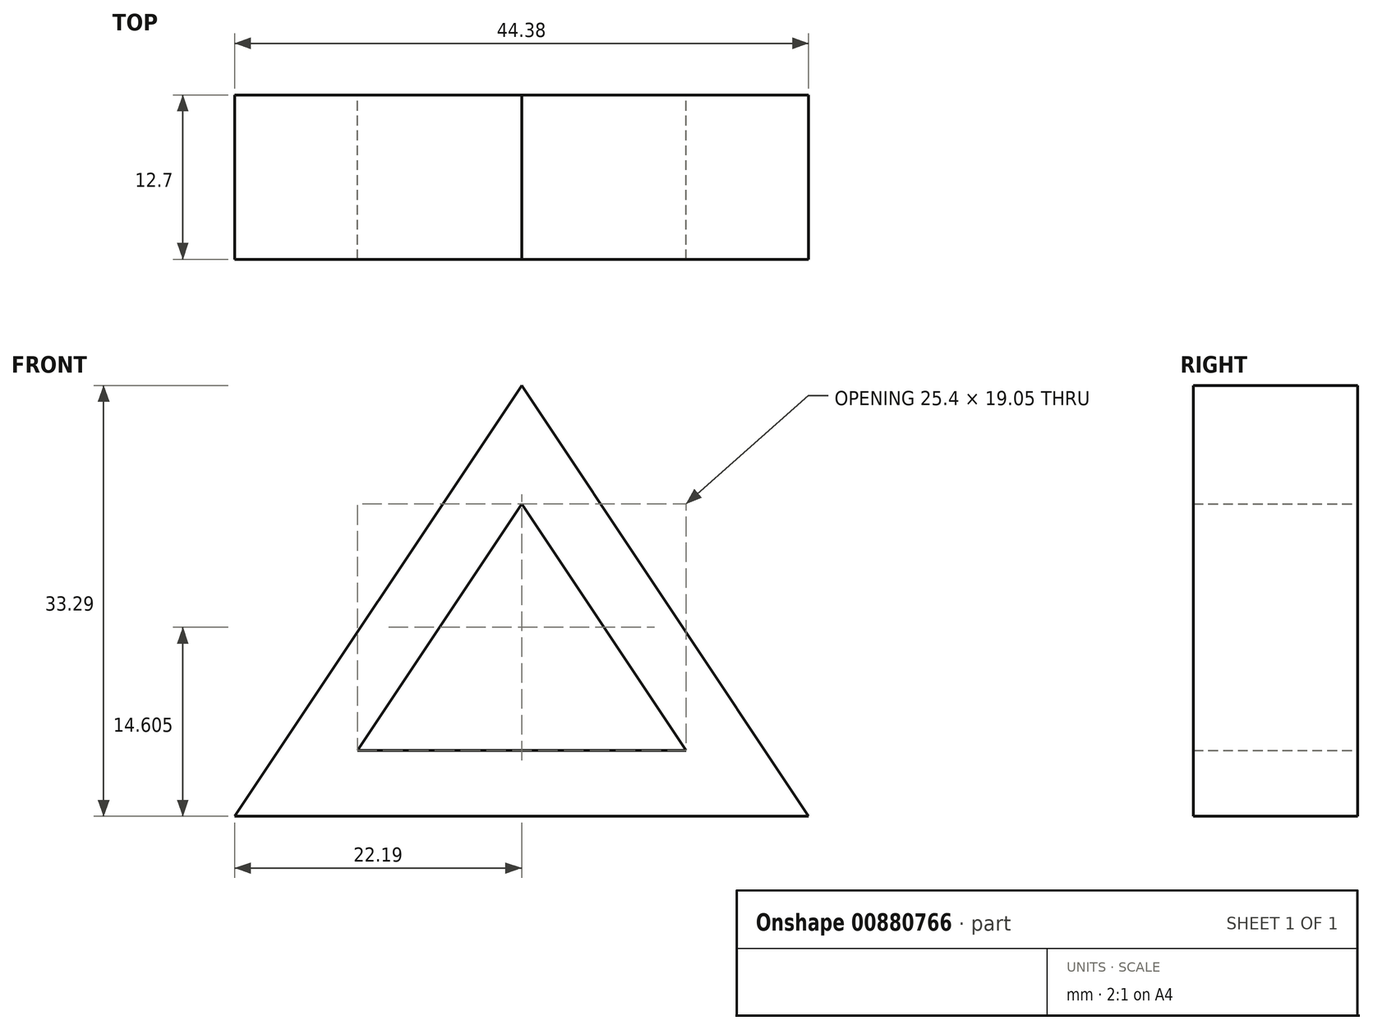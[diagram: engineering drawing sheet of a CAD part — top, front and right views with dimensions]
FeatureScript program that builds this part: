
annotation { "Feature Type Name" : "Feature", "Feature Type Description" : "" }
export const myFeature = defineFeature(function(context is Context, id is Id, definition is map)
    precondition{}
    {
        {
            var Q0;
            Q0=qCreatedBy(makeId("Front.planeOp"),FACE);
            var sketch = newSketch(context, id + "F0", { "sketchPlane" : qUnion([Q0])});
            skLineSegment(sketch, "E0", {"start": v(-12.7, 0) * mm, "end": v(0, 19.05) * mm});
            skLineSegment(sketch, "E1.MirrorCS", {"start": v(12.7, 0) * mm, "end": v(0, 19.05) * mm});
            skLineSegment(sketch, "E2", {"start": v(0, 0) * mm, "end": v(-12.7, 0) * mm});
            skLineSegment(sketch, "E3.MirrorCS", {"start": v(0, 0) * mm, "end": v(12.7, 0) * mm});
            skLineSegment(sketch, "E4", {"start": v(-22.2, -5.08) * mm, "end": v(0, 28.2) * mm});
            skPoint(sketch, "E5.orphan", {"position": v(-18.8, 0) * mm});
            skPoint(sketch, "E6.start.orphan", {"position": v(0, -5.08) * mm});
            skLineSegment(sketch, "E7", {"start": v(0, -5.08) * mm, "end": v(-22.2, -5.08) * mm});
            skLineSegment(sketch, "E8.MirrorCS", {"start": v(22.2, -5.08) * mm, "end": v(0, 28.2) * mm});
            skLineSegment(sketch, "E9.MirrorCS", {"start": v(0, -5.08) * mm, "end": v(22.2, -5.08) * mm});
            skSolve(sketch);
        }
        {
            var Q0;
            Q0=makeQuery(id+"F0.imprint","IMPRINT",FACE,{"disambiguationData":[TD([[makeQuery(id+"F0.imprint","IMPRINT",EDGE,{"derivedFrom":sQuery(id+"F0.wireOp",EDGE,"E0")}),1.0]])]});
            extrude(context, id + "F1", {"entities" : qUnion([Q0]), "depth" : 12.7 * mm, "offsetDistance" : 25.4 * mm});
        }
    });
